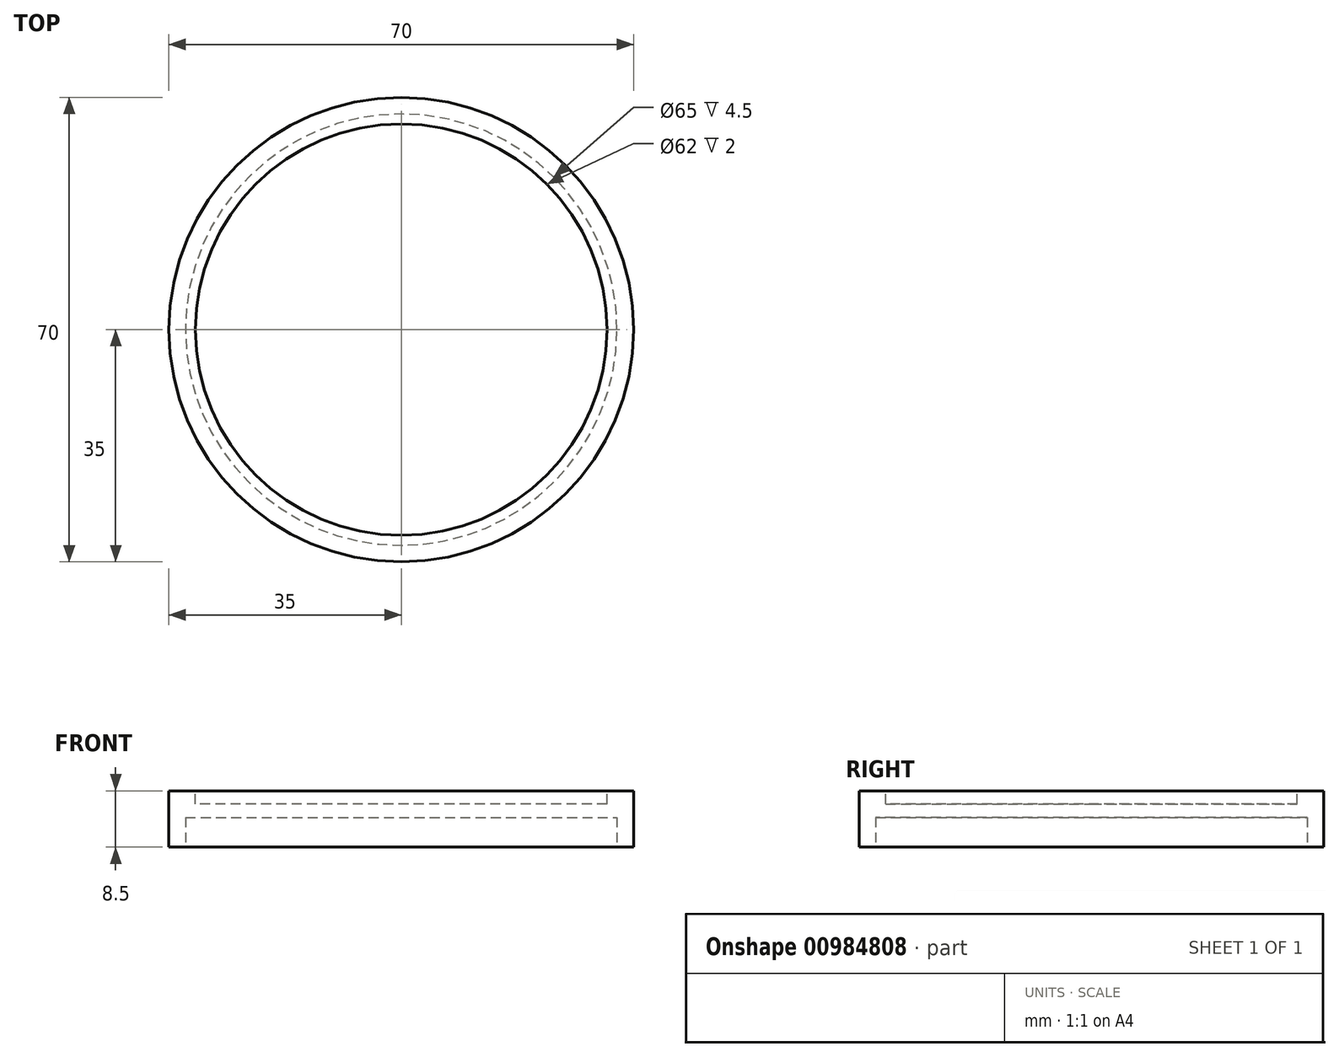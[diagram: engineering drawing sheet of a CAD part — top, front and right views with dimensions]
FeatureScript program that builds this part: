
annotation { "Feature Type Name" : "Feature", "Feature Type Description" : "" }
export const myFeature = defineFeature(function(context is Context, id is Id, definition is map)
    precondition{}
    {
        {
            var Q0;
            Q0=qCreatedBy(makeId("Front.planeOp"),FACE);
            var sketch = newSketch(context, id + "F0", { "sketchPlane" : qUnion([Q0])});
            skLineSegment(sketch, "E0.bottom", {"start": v(32.5, 0) * mm, "end": v(35, 0) * mm});
            skLineSegment(sketch, "E0.top", {"start": v(0, 8.5) * mm, "end": v(35, 8.5) * mm});
            skLineSegment(sketch, "E0.right", {"start": v(35, 0) * mm, "end": v(35, 8.5) * mm});
            skLineSegment(sketch, "E1", {"start": v(0, 4.5) * mm, "end": v(32.5, 4.5) * mm});
            skLineSegment(sketch, "E2", {"start": v(32.5, 4.5) * mm, "end": v(32.5, 0) * mm});
            skLineSegment(sketch, "E3", {"start": v(0, 4.5) * mm, "end": v(0, 8.5) * mm});
            skLineSegment(sketch, "E4", {"start": v(0, 0) * mm, "end": v(0, 16.47) * mm, "construction": true});
            skSolve(sketch);
        }
        {
            var Q0;
            Q0 = qSketchRegion(id + "F0", true);
            var Q1;
            Q1=sQuery(id+"F0.wireOp",EDGE,"E4");
            revolve(context, id + "F1", {"surfaceOperationType" : NewSurfaceOperationType.NEW, "entities" : qUnion([Q0]), "axis" : qUnion([Q1]), "revolveType" : RevolveType.FULL});
        }
        {
            var Q0;
            Q0=makeQuery(id+"F1.opRevolve","SWEPT_FACE",FACE,{"disambiguationData":[OSD([sQuery(id+"F0.wireOp",EDGE,"E0.top")])]});
            var sketch = newSketch(context, id + "F2", { "sketchPlane" : qUnion([Q0])});
            skCircle(sketch, "E5", {"center": v(0, 0) * mm, "radius": 31 * mm});
            skSolve(sketch);
        }
        {
            var Q0;
            Q0=makeQuery(id+"F2.imprint","IMPRINT",FACE,{"disambiguationData":[TD([[makeQuery(id+"F2.imprint","IMPRINT",EDGE,{"derivedFrom":sQuery(id+"F2.wireOp",EDGE,"E5")}),1.0]])]});
            extrude(context, id + "F3", {"entities" : qUnion([Q0]), "operationType" : NewBodyOperationType.REMOVE, "oppositeDirection" : true, "depth" : 2 * mm, "offsetDistance" : 25 * mm});
        }
    });
